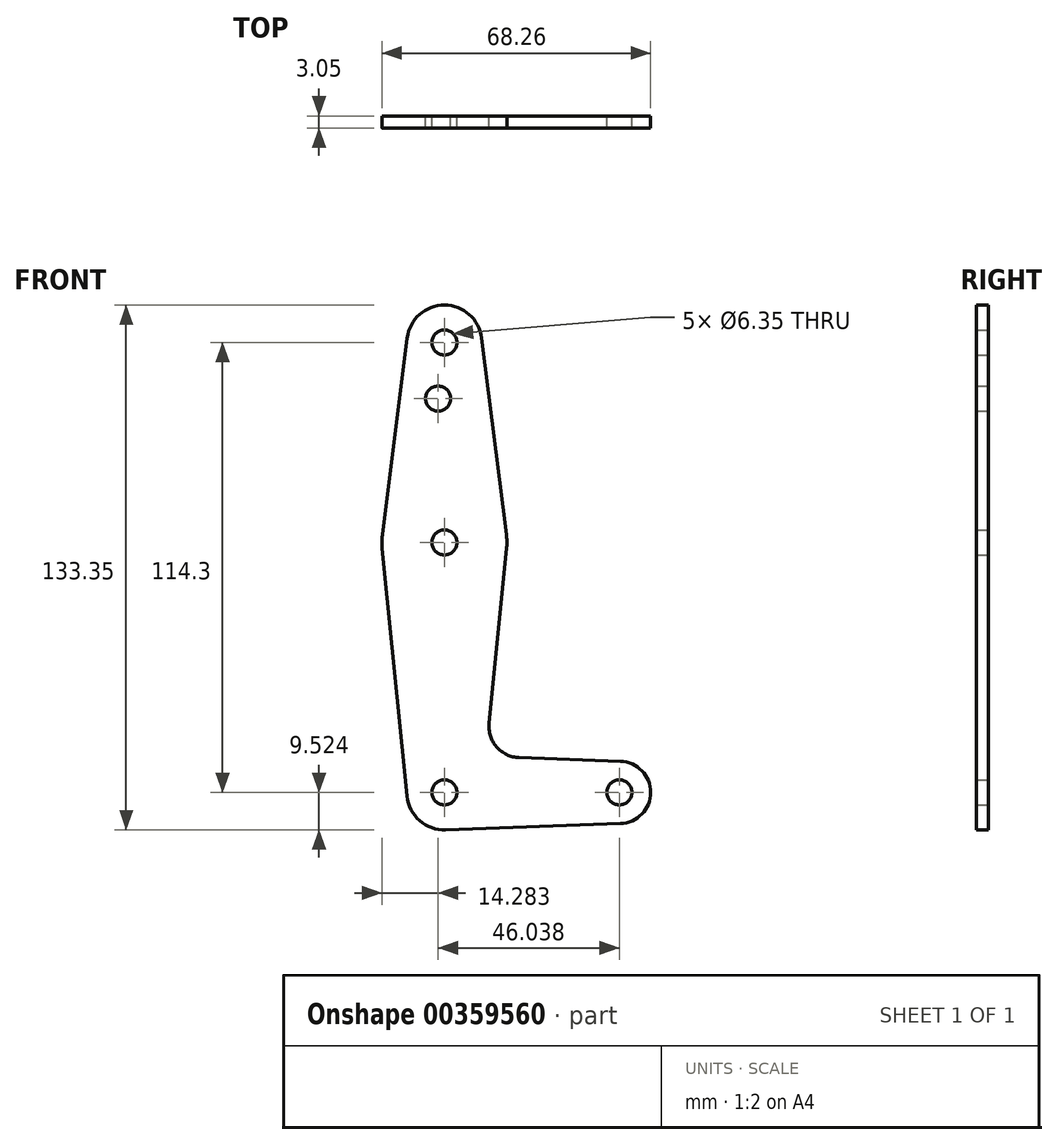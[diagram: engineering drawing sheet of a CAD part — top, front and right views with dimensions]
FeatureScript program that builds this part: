
annotation { "Feature Type Name" : "Feature", "Feature Type Description" : "" }
export const myFeature = defineFeature(function(context is Context, id is Id, definition is map)
    precondition{}
    {
        {
            var Q0;
            Q0=qCreatedBy(makeId("Front.planeOp"),FACE);
            var sketch = newSketch(context, id + "F0", { "sketchPlane" : qUnion([Q0])});
            skLineSegment(sketch, "E0", {"start": v(-28.78, 57.66) * mm, "end": v(-28.78, -56.64) * mm, "construction": true});
            skLineSegment(sketch, "E1", {"start": v(-28.78, -56.64) * mm, "end": v(15.67, -56.64) * mm, "construction": true});
            skCircle(sketch, "E2", {"center": v(-28.78, 57.66) * mm, "radius": 9.53 * mm});
            skCircle(sketch, "E3", {"center": v(-28.78, 6.86) * mm, "radius": 15.88 * mm});
            skCircle(sketch, "E4", {"center": v(-28.78, -56.64) * mm, "radius": 9.53 * mm});
            skCircle(sketch, "E5", {"center": v(15.67, -56.64) * mm, "radius": 7.94 * mm});
            skLineSegment(sketch, "E6", {"start": v(-38.26, -57.59) * mm, "end": v(-44.57, 5.28) * mm});
            skLineSegment(sketch, "E7", {"start": v(-12.98, 5.28) * mm, "end": v(-17.44, -39.05) * mm});
            skLineSegment(sketch, "E8", {"start": v(-38.23, 58.85) * mm, "end": v(-44.53, 8.85) * mm});
            skLineSegment(sketch, "E9", {"start": v(-19.33, 58.85) * mm, "end": v(-13.03, 8.85) * mm});
            skLineSegment(sketch, "E10", {"start": v(-28.44, -66.16) * mm, "end": v(15.95, -64.57) * mm});
            skLineSegment(sketch, "E11", {"start": v(-9.81, -47.79) * mm, "end": v(15.95, -48.7) * mm});
            skCircle(sketch, "E12", {"center": v(-28.78, 57.66) * mm, "radius": 3.18 * mm});
            skCircle(sketch, "E13", {"center": v(-28.78, 6.86) * mm, "radius": 3.18 * mm});
            skCircle(sketch, "E14", {"center": v(-28.78, -56.64) * mm, "radius": 3.18 * mm});
            skCircle(sketch, "E15", {"center": v(15.67, -56.64) * mm, "radius": 3.18 * mm});
            skCircle(sketch, "E16", {"center": v(-30.37, 43.43) * mm, "radius": 3.18 * mm});
            skArc(sketch, "E17.filletArc", {"start": v(-17.44, -39.05) * mm, "mid": v(-15.52, -45.07) * mm, "end": v(-9.81, -47.79) * mm});
            skSolve(sketch);
        }
        {
            var Q0;
            Q0 = qSketchRegion(id + "F0", true);
            extrude(context, id + "F1", {"entities" : qUnion([Q0]), "depth" : 3.05 * mm});
        }
    });
